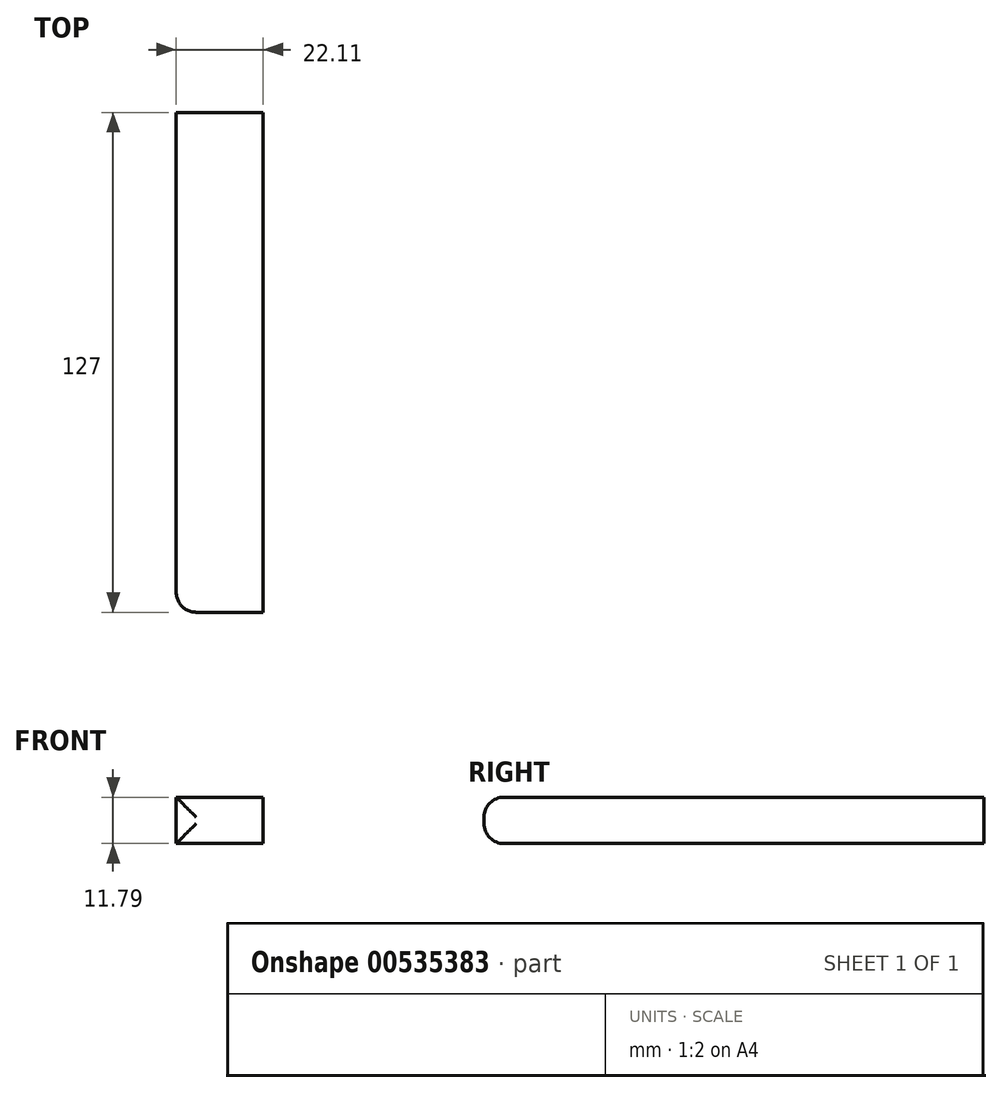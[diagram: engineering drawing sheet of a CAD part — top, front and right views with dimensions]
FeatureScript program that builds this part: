
annotation { "Feature Type Name" : "Feature", "Feature Type Description" : "" }
export const myFeature = defineFeature(function(context is Context, id is Id, definition is map)
    precondition{}
    {
        {
            var Q0;
            Q0=qCreatedBy(makeId("Front.planeOp"),FACE);
            var sketch = newSketch(context, id + "F0", { "sketchPlane" : qUnion([Q0])});
            skLineSegment(sketch, "E0.left", {"start": v(0, 0) * mm, "end": v(0, 11.8) * mm});
            skLineSegment(sketch, "E0.right", {"start": v(-304.8, 0) * mm, "end": v(-304.8, 11.8) * mm});
            skLineSegment(sketch, "E1.left", {"start": v(-304.8, -12.63) * mm, "end": v(-304.8, 0) * mm});
            skLineSegment(sketch, "E2.top", {"start": v(0, 11.8) * mm, "end": v(-22.1, 11.8) * mm});
            skLineSegment(sketch, "E2.right", {"start": v(-22.1, 0) * mm, "end": v(-22.1, 11.8) * mm});
            skLineSegment(sketch, "E3", {"start": v(-22.1, 0) * mm, "end": v(0, 0) * mm});
            skSolve(sketch);
        }
        {
            var Q0;
            Q0=makeQuery(id+"F0.imprint","IMPRINT",FACE,{"disambiguationData":[TD([[makeQuery(id+"F0.imprint","IMPRINT",EDGE,{"derivedFrom":sQuery(id+"F0.wireOp",EDGE,"E2.top")}),1.0]])]});
            extrude(context, id + "F1", {"entities" : qUnion([Q0]), "depth" : 127 * mm, "offsetDistance" : 25.4 * mm});
        }
        {
            var Q0;
            Q0=makeQuery(id+"F1.opExtrude","CAP_FACE",FACE,{"disambiguationData":[OSD([sQuery(id+"F0.wireOp",EDGE,"E2.top"),sQuery(id+"F0.wireOp",EDGE,"E0.left"),sQuery(id+"F0.wireOp",EDGE,"E2.right"),sQuery(id+"F0.wireOp",EDGE,"E3")])],"isStart":true});
            extrude(context, id + "F2", {"entities" : qUnion([Q0]), "operationType" : NewBodyOperationType.ADD, "oppositeDirection" : true, "depth" : 101.6 * mm, "offsetDistance" : 25.4 * mm});
        }
        {
            var Q0;
            Q0=makeQuery(id+"F1.opExtrude","CAP_EDGE",EDGE,{"disambiguationData":[OSD([sQuery(id+"F0.wireOp",EDGE,"E2.top")])],"isStart":false});
            var Q1;
            Q1=makeQuery(id+"F1.opExtrude","CAP_EDGE",EDGE,{"disambiguationData":[OSD([sQuery(id+"F0.wireOp",EDGE,"E2.right")])],"isStart":false});
            var Q2;
            Q2=makeQuery(id+"F1.opExtrude","CAP_EDGE",EDGE,{"disambiguationData":[OSD([sQuery(id+"F0.wireOp",EDGE,"E0.left")])],"isStart":false});
            var Q3;
            Q3=makeQuery(id+"F1.opExtrude","CAP_EDGE",EDGE,{"disambiguationData":[OSD([sQuery(id+"F0.wireOp",EDGE,"E3")])],"isStart":false});
            fillet(context, id + "F3", {"entities" : qUnion([Q0, Q1, Q2, Q3]), "radius" : 5.08 * mm, "tangentPropagation" : true, "allowEdgeOverflow" : false});
        }
    });
